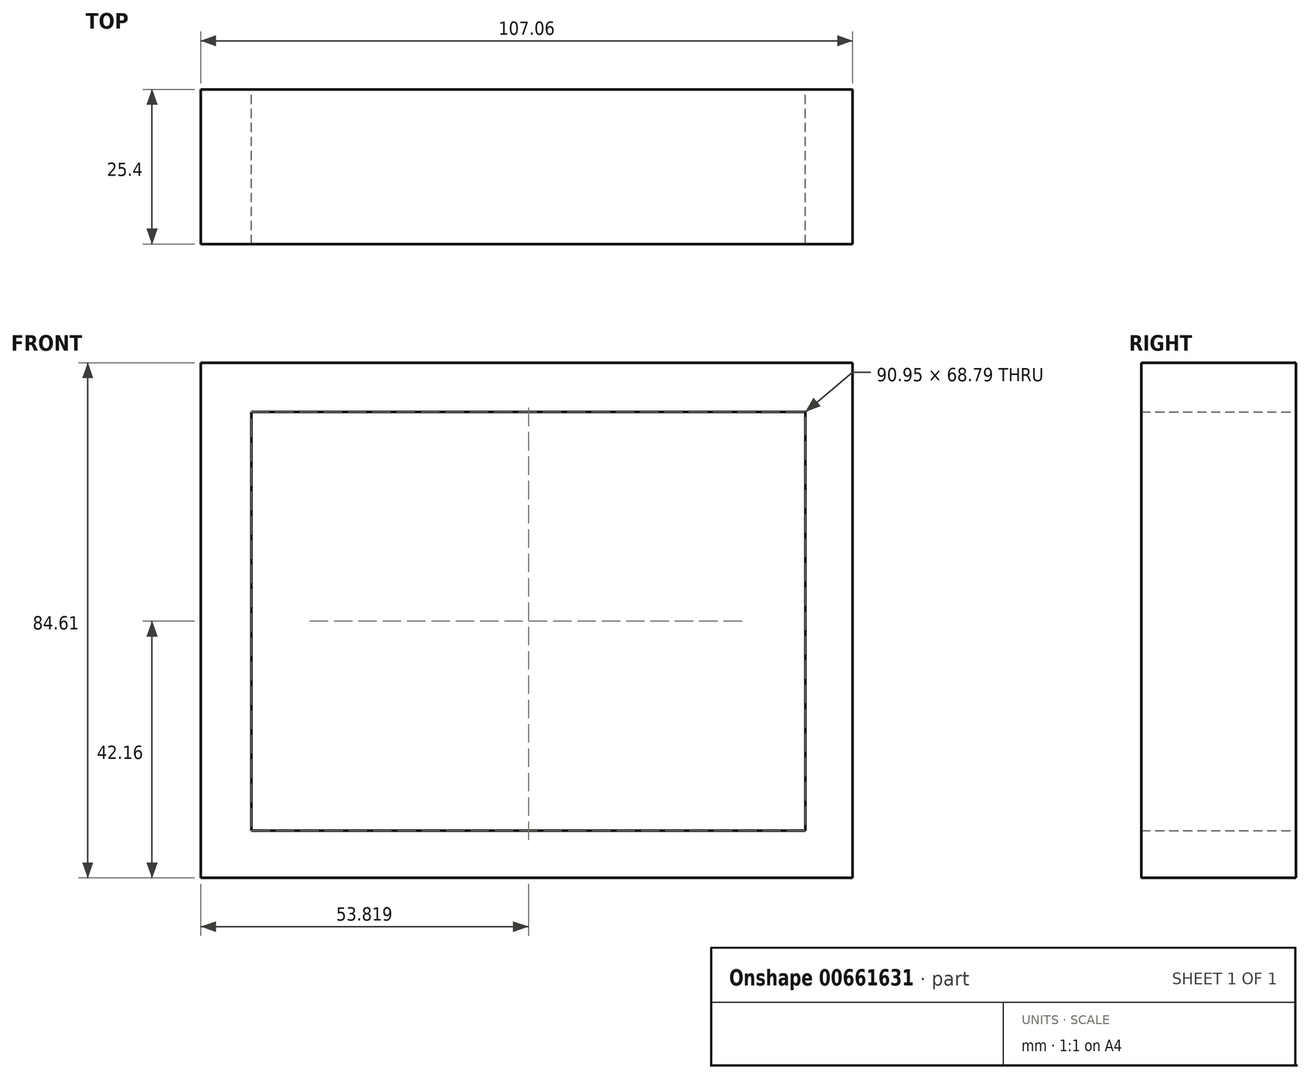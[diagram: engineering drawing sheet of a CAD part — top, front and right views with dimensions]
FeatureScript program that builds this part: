
annotation { "Feature Type Name" : "Feature", "Feature Type Description" : "" }
export const myFeature = defineFeature(function(context is Context, id is Id, definition is map)
    precondition{}
    {
        {
            var Q0;
            Q0=qCreatedBy(makeId("Front.planeOp"),FACE);
            var sketch = newSketch(context, id + "F0", { "sketchPlane" : qUnion([Q0])});
            skLineSegment(sketch, "E0.bottom", {"start": v(-55.7, 37.27) * mm, "end": v(51.37, 37.27) * mm});
            skLineSegment(sketch, "E0.top", {"start": v(-55.7, -47.34) * mm, "end": v(51.37, -47.34) * mm});
            skLineSegment(sketch, "E0.left", {"start": v(-55.7, 37.27) * mm, "end": v(-55.7, -47.34) * mm});
            skLineSegment(sketch, "E0.right", {"start": v(51.37, 37.27) * mm, "end": v(51.37, -47.34) * mm});
            skLineSegment(sketch, "E1.bottom", {"start": v(-47.34, 29.21) * mm, "end": v(43.6, 29.21) * mm});
            skLineSegment(sketch, "E1.top", {"start": v(-47.34, -39.57) * mm, "end": v(43.6, -39.57) * mm});
            skLineSegment(sketch, "E1.left", {"start": v(-47.34, 29.21) * mm, "end": v(-47.34, -39.57) * mm});
            skLineSegment(sketch, "E1.right", {"start": v(43.6, 29.21) * mm, "end": v(43.6, -39.57) * mm});
            skSolve(sketch);
        }
        {
            var Q0;
            Q0=makeQuery(id+"F0.imprint","IMPRINT",FACE,{"disambiguationData":[TD([[makeQuery(id+"F0.imprint","IMPRINT",EDGE,{"derivedFrom":sQuery(id+"F0.wireOp",EDGE,"E0.bottom")}),-1.0]])]});
            extrude(context, id + "F1", {"entities" : qUnion([Q0]), "depth" : 25.4 * mm, "offsetDistance" : 25.4 * mm});
        }
    });
